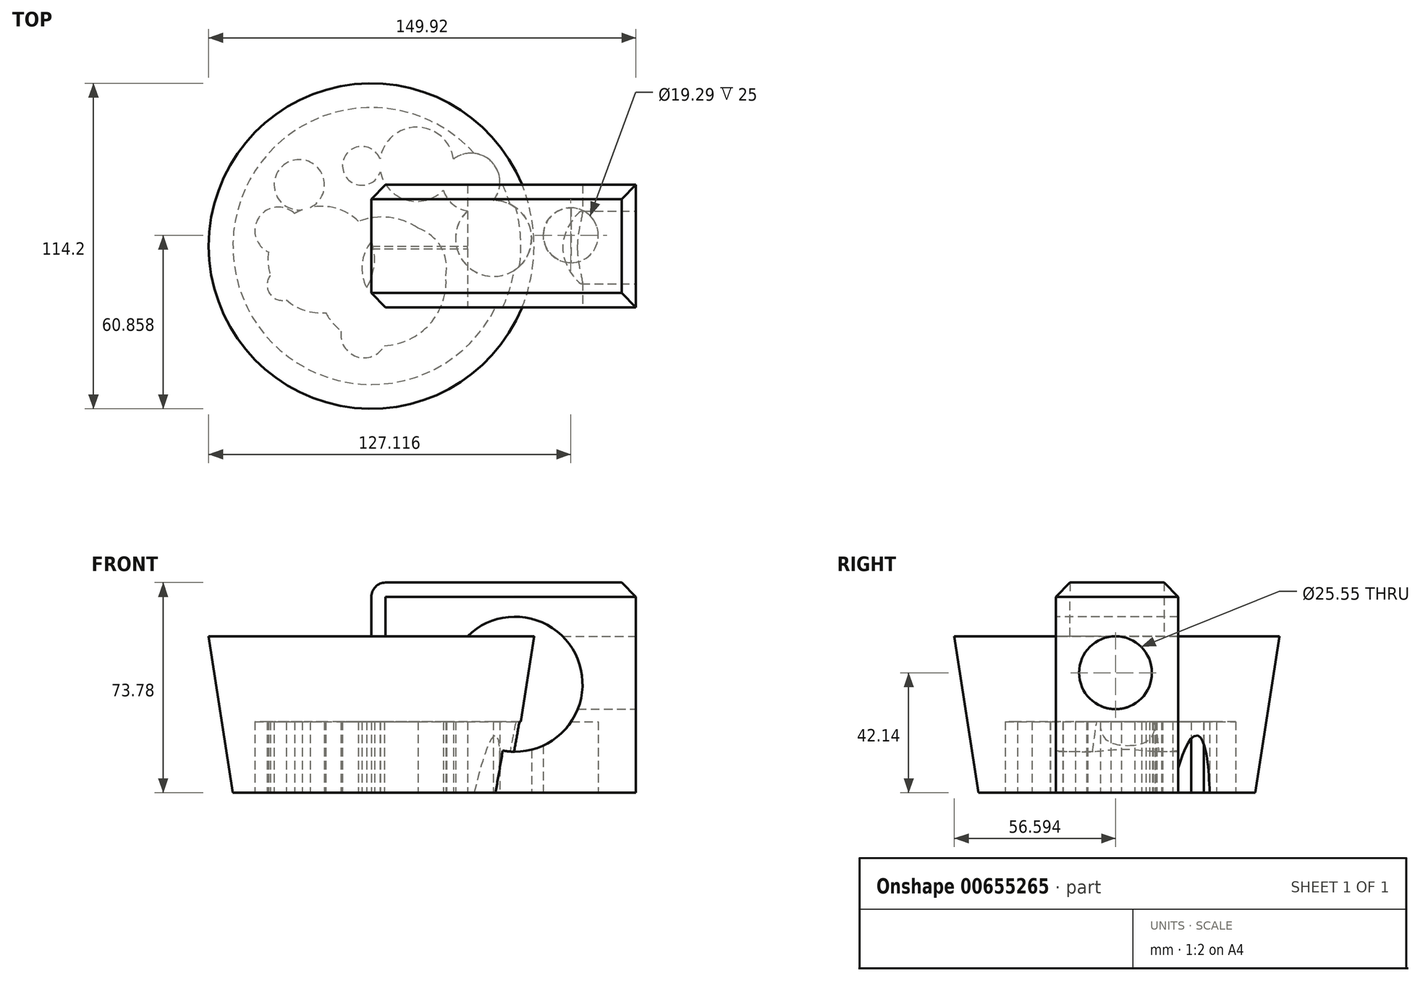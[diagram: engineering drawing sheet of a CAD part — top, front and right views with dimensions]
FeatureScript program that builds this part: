
annotation { "Feature Type Name" : "Feature", "Feature Type Description" : "" }
export const myFeature = defineFeature(function(context is Context, id is Id, definition is map)
    precondition{}
    {
        {
            var Q0;
            Q0=qCreatedBy(makeId("Front.planeOp"),FACE);
            var sketch = newSketch(context, id + "F0", { "sketchPlane" : qUnion([Q0])});
            skLineSegment(sketch, "E0.bottom", {"start": v(0, 0) * mm, "end": v(-92.83, 0) * mm});
            skLineSegment(sketch, "E0.top", {"start": v(0, 73.78) * mm, "end": v(-92.83, 73.78) * mm});
            skLineSegment(sketch, "E0.left", {"start": v(0, 0) * mm, "end": v(0, 73.78) * mm});
            skLineSegment(sketch, "E0.right", {"start": v(-92.83, 0) * mm, "end": v(-92.83, 73.78) * mm});
            skSolve(sketch);
        }
        {
            var Q0;
            Q0 = qSketchRegion(id + "F0", true);
            extrude(context, id + "F1", {"entities" : qUnion([Q0]), "depth" : 43 * mm, "offsetDistance" : 25 * mm});
        }
        {
            var Q0;
            Q0=makeQuery(id+"F1.opExtrude","SWEPT_EDGE",EDGE,{"disambiguationData":[OSD([sQuery(id+"F0.wireOp",EDGE,"E0.top"),sQuery(id+"F0.wireOp",EDGE,"E0.right")])]});
            fillet(context, id + "F2", {"entities" : qUnion([Q0]), "radius" : 5 * mm, "tangentPropagation" : true, "allowEdgeOverflow" : false});
        }
        {
            var Q0;
            Q0=makeQuery(id+"F1.opExtrude","SWEPT_FACE",FACE,{"disambiguationData":[OSD([sQuery(id+"F0.wireOp",EDGE,"E0.top")])]});
            chamfer(context, id + "F3", {"entities" : qUnion([Q0]), "width" : 5 * mm, "tangentPropagation" : true});
        }
        {
            var Q0;
            Q0=makeQuery(id+"F1.opExtrude","CAP_FACE",FACE,{"disambiguationData":[OSD([sQuery(id+"F0.wireOp",EDGE,"E0.bottom"),sQuery(id+"F0.wireOp",EDGE,"E0.top"),sQuery(id+"F0.wireOp",EDGE,"E0.left"),sQuery(id+"F0.wireOp",EDGE,"E0.right")])],"isStart":false});
            var sketch = newSketch(context, id + "F4", { "sketchPlane" : qUnion([Q0])});
            skCircle(sketch, "E1", {"center": v(-42.4, 38.1) * mm, "radius": 23.69 * mm});
            skSolve(sketch);
        }
        {
            var Q0;
            Q0 = qSketchRegion(id + "F4", true);
            extrude(context, id + "F5", {"entities" : qUnion([Q0]), "operationType" : NewBodyOperationType.REMOVE, "oppositeDirection" : true, "depth" : 58.1 * mm, "offsetDistance" : 25 * mm});
        }
        {
            var Q0;
            Q0=makeQuery(id+"F1.opExtrude","SWEPT_FACE",FACE,{"disambiguationData":[OSD([sQuery(id+"F0.wireOp",EDGE,"E0.left")])]});
            var sketch = newSketch(context, id + "F6", { "sketchPlane" : qUnion([Q0])});
            skCircle(sketch, "E2", {"center": v(-22, 42.14) * mm, "radius": 12.78 * mm});
            skSolve(sketch);
        }
        {
            var Q0;
            Q0 = qSketchRegion(id + "F6", true);
            extrude(context, id + "F7", {"entities" : qUnion([Q0]), "operationType" : NewBodyOperationType.REMOVE, "oppositeDirection" : true, "depth" : 105 * mm, "offsetDistance" : 25 * mm});
        }
        {
            var Q0;
            Q0=makeQuery(id+"F1.opExtrude","SWEPT_FACE",FACE,{"disambiguationData":[OSD([sQuery(id+"F0.wireOp",EDGE,"E0.right")])]});
            var sketch = newSketch(context, id + "F8", { "sketchPlane" : qUnion([Q0])});
            skLineSegment(sketch, "E3", {"start": v(21.5, 0) * mm, "end": v(21.5, 54.9) * mm});
            skLineSegment(sketch, "E4", {"start": v(21.5, 54.9) * mm, "end": v(78.6, 54.9) * mm});
            skLineSegment(sketch, "E5", {"start": v(78.6, 54.9) * mm, "end": v(70.1, 0) * mm});
            skLineSegment(sketch, "E6", {"start": v(70.1, 0) * mm, "end": v(21.5, 0) * mm});
            skSolve(sketch);
        }
        {
            var Q0;
            Q0 = qSketchRegion(id + "F8", true);
            var Q1;
            Q1=sQuery(id+"F8.wireOp",EDGE,"E3");
            revolve(context, id + "F9", {"operationType" : NewBodyOperationType.ADD, "entities" : qUnion([Q0]), "axis" : qUnion([Q1]), "revolveType" : RevolveType.FULL});
        }
        {
            var Q0;
            Q0=makeQuery(id+"F9.boolean.opBoolean","MERGE",FACE,{"derivedFrom":[makeQuery(id+"F1.opExtrude","SWEPT_FACE",FACE,{"disambiguationData":[OSD([sQuery(id+"F0.wireOp",EDGE,"E0.bottom")])]}),makeQuery(id+"F9.opRevolve","SWEPT_FACE",FACE,{"disambiguationData":[OSD([sQuery(id+"F8.wireOp",EDGE,"E6")])]})]});
            var sketch = newSketch(context, id + "F10", { "sketchPlane" : qUnion([Q0])});
            skCircle(sketch, "E7", {"center": v(-95.4, 52.58) * mm, "radius": 8.14 * mm});
            skCircle(sketch, "E8", {"center": v(-124, 35.16) * mm, "radius": 5.43 * mm});
            skCircle(sketch, "E9", {"center": v(-125.47, 16.1) * mm, "radius": 8.26 * mm});
            skCircle(sketch, "E10", {"center": v(-118.14, 0) * mm, "radius": 8.84 * mm});
            skCircle(sketch, "E11", {"center": v(-96.14, -6.64) * mm, "radius": 6.8 * mm});
            skCircle(sketch, "E12", {"center": v(-76.89, -7.2) * mm, "radius": 13.02 * mm});
            skCircle(sketch, "E13", {"center": v(-57.82, -0.96) * mm, "radius": 10.12 * mm});
            skCircle(sketch, "E14", {"center": v(-49.94, 18.84) * mm, "radius": 13.33 * mm});
            skCircle(sketch, "E15", {"center": v(-22.8, 17.74) * mm, "radius": 9.65 * mm});
            skCircle(sketch, "E16", {"center": v(-89.17, 33.88) * mm, "radius": 22.57 * mm});
            skCircle(sketch, "E17", {"center": v(-110.42, 26.25) * mm, "radius": 18.71 * mm});
            skCircle(sketch, "E18", {"center": v(-81.29, 29.3) * mm, "radius": 14.86 * mm});
            skSolve(sketch);
        }
        {
            var Q0;
            Q0 = qSketchRegion(id + "F10", true);
            extrude(context, id + "F11", {"entities" : qUnion([Q0]), "operationType" : NewBodyOperationType.REMOVE, "oppositeDirection" : true, "depth" : 25 * mm, "offsetDistance" : 25 * mm});
        }
    });
